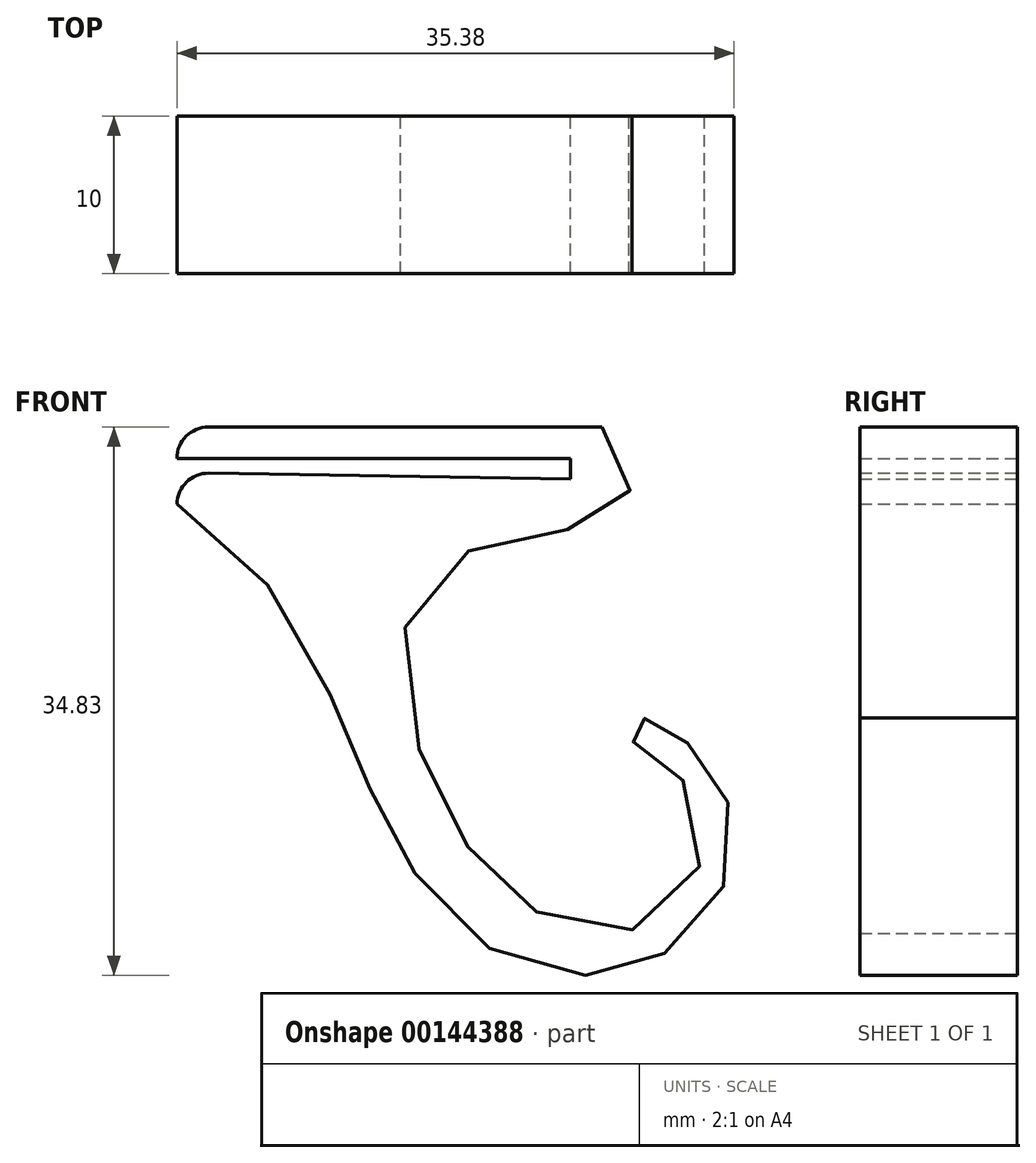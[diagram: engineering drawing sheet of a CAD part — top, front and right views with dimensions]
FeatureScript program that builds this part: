
annotation { "Feature Type Name" : "Feature", "Feature Type Description" : "" }
export const myFeature = defineFeature(function(context is Context, id is Id, definition is map)
    precondition{}
    {
        {
            var Q0;
            Q0=qCreatedBy(makeId("Front.planeOp"),FACE);
            var sketch = newSketch(context, id + "F0", { "sketchPlane" : qUnion([Q0])});
            skLineSegment(sketch, "E0", {"start": v(0, 0) * mm, "end": v(27, 0) * mm});
            skLineSegment(sketch, "E1", {"start": v(27, 0) * mm, "end": v(27, -4.9) * mm});
            skLineSegment(sketch, "E2", {"start": v(27, -4.9) * mm, "end": v(0, -4.9) * mm});
            skLineSegment(sketch, "E3", {"start": v(0, -4.9) * mm, "end": v(0, -2.9) * mm});
            skLineSegment(sketch, "E4", {"start": v(0, -2.9) * mm, "end": v(25, -3.3) * mm});
            skLineSegment(sketch, "E5", {"start": v(25, -3.3) * mm, "end": v(25, -2) * mm});
            skLineSegment(sketch, "E6", {"start": v(25, -2) * mm, "end": v(0, -2) * mm});
            skLineSegment(sketch, "E7", {"start": v(0, -2) * mm, "end": v(0, 0) * mm});
            skFitSpline(sketch, "E8", {"points": [v(0, -4.9) * mm, v(7.02, -11.72) * mm, v(10.72, -19.53) * mm, v(13.27, -25.02) * mm, v(16.47, -30.14) * mm, v(22.34, -34.33) * mm, v(27.87, -34.6) * mm, v(31.54, -33.05) * mm, v(34.8, -29) * mm, v(35.18, -24.47) * mm, v(33.46, -21.1) * mm, v(31.66, -19.49) * mm, v(30.36, -18.75) * mm, v(29.4, -18.5) * mm, v(28.87, -18.97) * mm, v(28.75, -19.74) * mm, v(29.43, -20.25) * mm, v(31.58, -21.78) * mm, v(33.5, -26.12) * mm, v(31.06, -30.9) * mm, v(25.54, -31.96) * mm, v(20.06, -28.57) * mm, v(17.02, -24.16) * mm, v(14.2, -14.93) * mm, v(17.1, -8.67) * mm, v(23.2, -6.76) * mm, v(27.84, -5.39) * mm, v(28.87, -2.7) * mm, v(27, 0) * mm], "startDerivative": vector(107.8, -48.98) * mm, "endDerivative": vector(-89.48, 0) * mm});
            skSolve(sketch);
        }
        {
            var Q0;
            Q0=makeQuery(id+"F0.imprint","IMPRINT",FACE,{"disambiguationData":[TD([[makeQuery(id+"F0.imprint","IMPRINT",EDGE,{"derivedFrom":sQuery(id+"F0.wireOp",EDGE,"E1")}),1.0]])]});
            var Q1;
            Q1=makeQuery(id+"F0.imprint","IMPRINT",FACE,{"disambiguationData":[TD([[makeQuery(id+"F0.imprint","IMPRINT",EDGE,{"derivedFrom":sQuery(id+"F0.wireOp",EDGE,"E0")}),-1.0]])]});
            extrude(context, id + "F1", {"entities" : qUnion([Q0, Q1]), "depth" : 10 * mm});
        }
        {
            var Q0;
            Q0=makeQuery(id+"F1.opExtrude","SWEPT_EDGE",EDGE,{"disambiguationData":[OSD([sQuery(id+"F0.wireOp",EDGE,"E0"),sQuery(id+"F0.wireOp",EDGE,"E7")])]});
            var Q1;
            Q1=makeQuery(id+"F1.opExtrude","SWEPT_EDGE",EDGE,{"disambiguationData":[OSD([sQuery(id+"F0.wireOp",EDGE,"E3"),sQuery(id+"F0.wireOp",EDGE,"E4")])]});
            fillet(context, id + "F2", {"entities" : qUnion([Q0, Q1]), "radius" : 2 * mm, "tangentPropagation" : true, "allowEdgeOverflow" : false});
        }
    });
